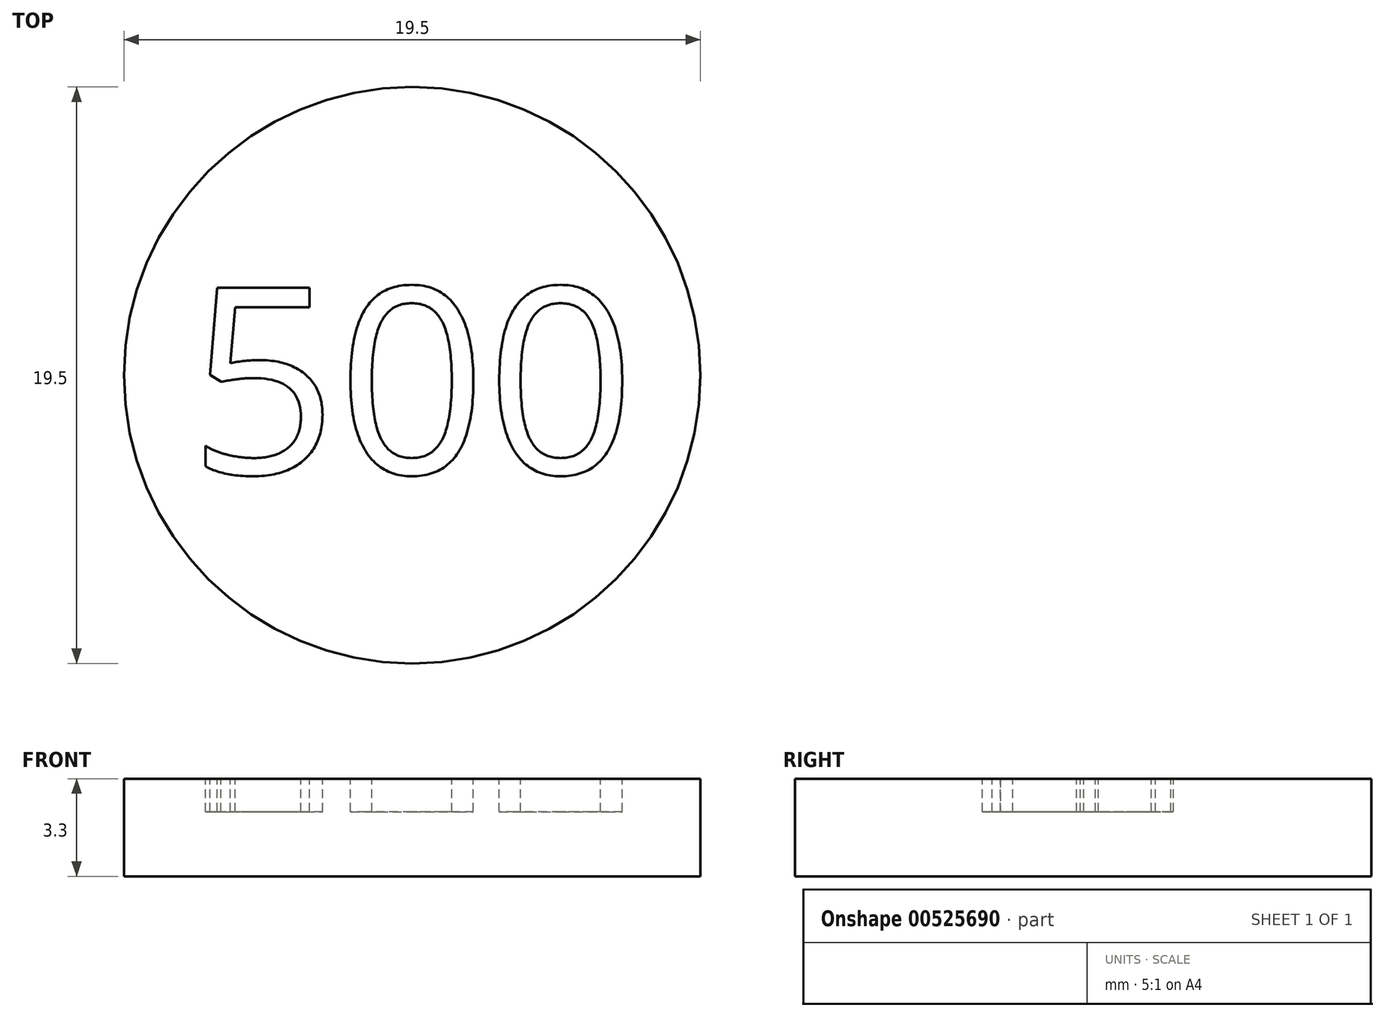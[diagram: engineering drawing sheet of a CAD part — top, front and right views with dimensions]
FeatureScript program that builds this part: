
annotation { "Feature Type Name" : "Feature", "Feature Type Description" : "" }
export const myFeature = defineFeature(function(context is Context, id is Id, definition is map)
    precondition{}
    {
        {
            var Q0;
            Q0=qCreatedBy(makeId("Top.planeOp"),FACE);
            var sketch = newSketch(context, id + "F0", { "sketchPlane" : qUnion([Q0])});
            skCircle(sketch, "E0", {"center": v(0, 0) * mm, "radius": 9.75 * mm});
            skSolve(sketch);
        }
        {
            var Q0;
            Q0 = qSketchRegion(id + "F0", true);
            extrude(context, id + "F1", {"entities" : qUnion([Q0]), "depth" : 3.3 * mm, "offsetDistance" : 25.4 * mm});
        }
        {
            var Q0;
            Q0=makeQuery(id+"F1.opExtrude","CAP_FACE",FACE,{"disambiguationData":[OSD([sQuery(id+"F0.wireOp",EDGE,"E0")])],"isStart":false});
            var sketch = newSketch(context, id + "F2", { "sketchPlane" : qUnion([Q0])});
            skText(sketch, "E1", { "text": "500\n", "fontName": "OpenSans-Regular.ttf"});
            const initialGuessF2  = {"E1": [-0.00756, -0.00333, 1, 0, 0.00634]};
            skSetInitialGuess(sketch, initialGuessF2);
            skSolve(sketch);
        }
        {
            var Q0;
            Q0 = qSketchRegion(id + "F2", true);
            extrude(context, id + "F3", {"entities" : qUnion([Q0]), "operationType" : NewBodyOperationType.REMOVE, "oppositeDirection" : true, "depth" : 1.12 * mm, "offsetDistance" : 25.4 * mm});
        }
    });
